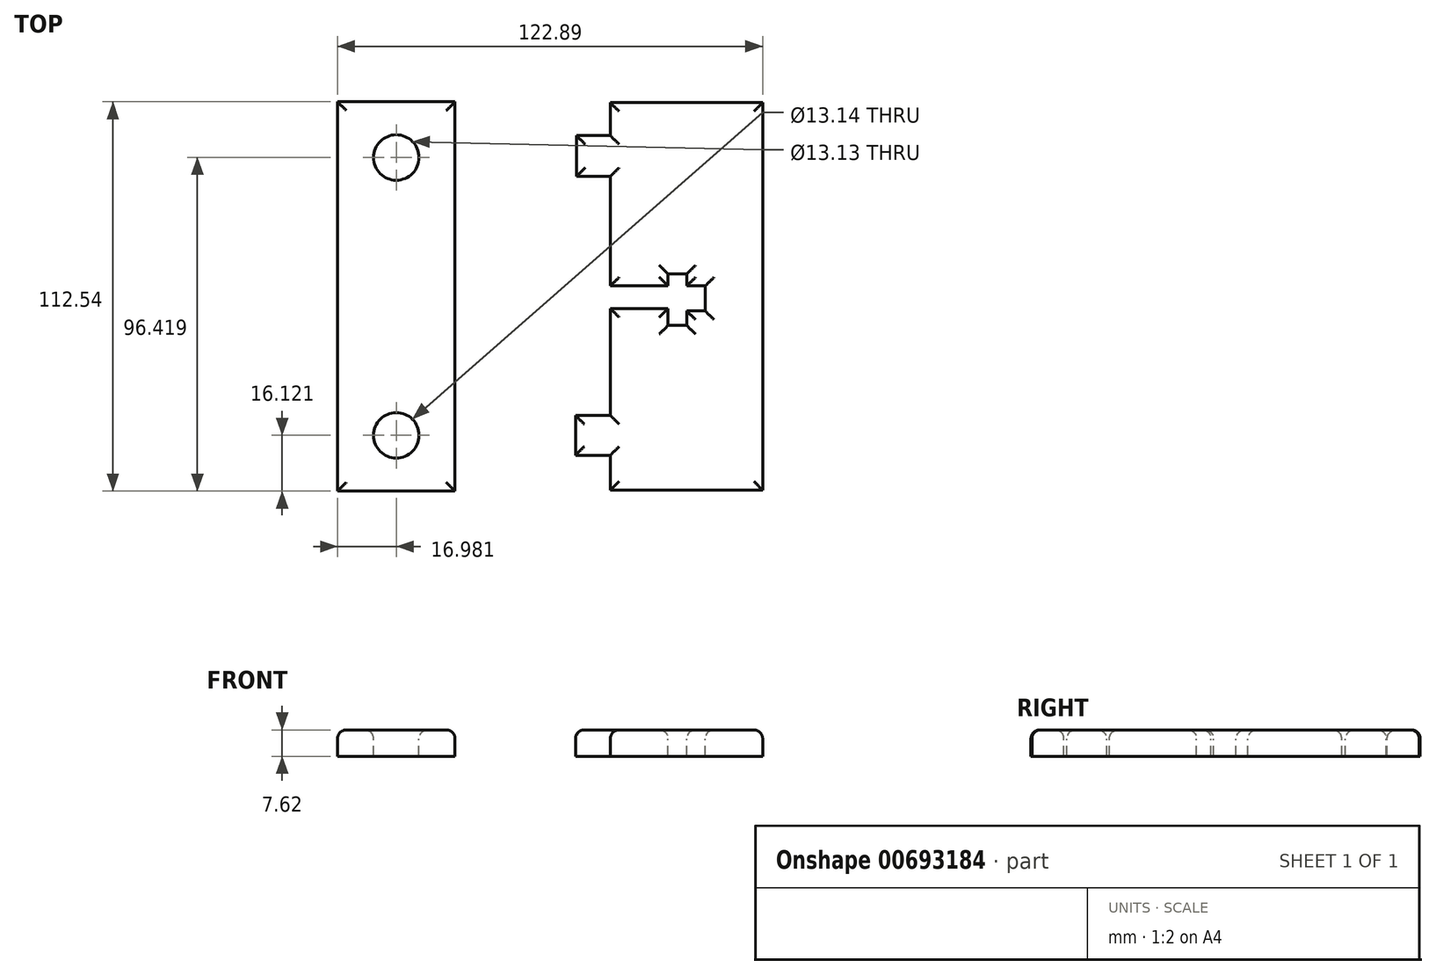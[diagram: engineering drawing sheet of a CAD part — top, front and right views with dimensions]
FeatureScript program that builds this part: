
annotation { "Feature Type Name" : "Feature", "Feature Type Description" : "" }
export const myFeature = defineFeature(function(context is Context, id is Id, definition is map)
    precondition{}
    {
        {
            var Q0;
            Q0=qCreatedBy(makeId("Top.planeOp"),FACE);
            var sketch = newSketch(context, id + "F0", { "sketchPlane" : qUnion([Q0])});
            skLineSegment(sketch, "E0.bottom", {"start": v(-59.72, 56.27) * mm, "end": v(-25.76, 56.27) * mm});
            skLineSegment(sketch, "E0.top", {"start": v(-59.72, -56.27) * mm, "end": v(-25.76, -56.27) * mm});
            skLineSegment(sketch, "E0.left", {"start": v(-59.72, 56.27) * mm, "end": v(-59.72, -56.27) * mm});
            skLineSegment(sketch, "E0.right", {"start": v(-25.76, 56.27) * mm, "end": v(-25.76, -56.27) * mm});
            skCircle(sketch, "E1", {"center": v(-42.74, -40.15) * mm, "radius": 6.57 * mm});
            skCircle(sketch, "E2", {"center": v(-42.74, 40.15) * mm, "radius": 6.56 * mm});
            skLineSegment(sketch, "E3.bottom", {"start": v(19.14, 55.98) * mm, "end": v(63.17, 55.98) * mm});
            skLineSegment(sketch, "E3.top", {"start": v(19.14, -55.98) * mm, "end": v(63.17, -55.98) * mm});
            skLineSegment(sketch, "E3.right", {"start": v(63.17, 55.98) * mm, "end": v(63.17, -55.98) * mm});
            skLineSegment(sketch, "E4", {"start": v(19.14, 46.48) * mm, "end": v(19.14, 55.98) * mm});
            skLineSegment(sketch, "E5", {"start": v(19.14, -55.98) * mm, "end": v(19.14, -45.9) * mm});
            skLineSegment(sketch, "E6", {"start": v(19.14, -45.9) * mm, "end": v(9.07, -45.9) * mm});
            skLineSegment(sketch, "E7", {"start": v(9.07, -45.9) * mm, "end": v(9.07, -34.4) * mm});
            skLineSegment(sketch, "E8", {"start": v(9.07, -34.4) * mm, "end": v(19.14, -34.4) * mm});
            skLineSegment(sketch, "E9", {"start": v(19.14, 46.48) * mm, "end": v(9.35, 46.48) * mm});
            skLineSegment(sketch, "E10", {"start": v(9.35, 46.48) * mm, "end": v(9.35, 34.68) * mm});
            skLineSegment(sketch, "E11", {"start": v(9.35, 34.68) * mm, "end": v(19.14, 34.68) * mm});
            skLineSegment(sketch, "E12", {"start": v(19.14, 3.02) * mm, "end": v(35.83, 3.02) * mm});
            skLineSegment(sketch, "E13", {"start": v(35.83, 3.02) * mm, "end": v(35.83, 6.48) * mm});
            skLineSegment(sketch, "E14", {"start": v(35.83, 6.48) * mm, "end": v(41.24, 6.48) * mm});
            skLineSegment(sketch, "E15", {"start": v(41.24, 6.48) * mm, "end": v(41.24, 3.02) * mm});
            skLineSegment(sketch, "E16", {"start": v(41.24, 3.02) * mm, "end": v(46.56, 3.02) * mm});
            skLineSegment(sketch, "E17", {"start": v(46.56, 3.02) * mm, "end": v(46.56, -2.33) * mm});
            skLineSegment(sketch, "E18", {"start": v(46.56, -2.33) * mm, "end": v(46.56, -4.2) * mm});
            skLineSegment(sketch, "E19", {"start": v(46.56, -4.2) * mm, "end": v(41.24, -4.2) * mm});
            skLineSegment(sketch, "E20", {"start": v(41.24, -4.2) * mm, "end": v(41.24, -8.37) * mm});
            skLineSegment(sketch, "E21", {"start": v(41.24, -8.37) * mm, "end": v(35.83, -8.37) * mm});
            skLineSegment(sketch, "E22", {"start": v(35.83, -8.37) * mm, "end": v(35.83, -3.48) * mm});
            skLineSegment(sketch, "E23", {"start": v(35.83, -3.48) * mm, "end": v(19.14, -3.48) * mm});
            skLineSegment(sketch, "E24", {"start": v(19.14, 3.02) * mm, "end": v(19.14, 34.68) * mm});
            skLineSegment(sketch, "E25", {"start": v(19.14, -3.48) * mm, "end": v(19.14, -34.4) * mm});
            skSolve(sketch);
        }
        {
            var Q0;
            Q0 = qSketchRegion(id + "F0", true);
            var Q1;
            Q1=qCreatedBy(makeId("Front.planeOp"),FACE);
            extrude(context, id + "F1", {"entities" : qUnion([Q0]), "oppositeDirection" : true, "depth" : 7.62 * mm, "endBoundEntityFace" : qUnion([Q1]), "offsetDistance" : 25.4 * mm});
        }
        {
            var Q0;
            Q0=makeQuery(id+"F1.opExtrude","CAP_FACE",FACE,{"disambiguationData":[OSD([sQuery(id+"F0.wireOp",EDGE,"E3.bottom"),sQuery(id+"F0.wireOp",EDGE,"E3.top"),sQuery(id+"F0.wireOp",EDGE,"E3.right"),sQuery(id+"F0.wireOp",EDGE,"E4"),sQuery(id+"F0.wireOp",EDGE,"E5"),sQuery(id+"F0.wireOp",EDGE,"E6"),sQuery(id+"F0.wireOp",EDGE,"E7"),sQuery(id+"F0.wireOp",EDGE,"E8"),sQuery(id+"F0.wireOp",EDGE,"E9"),sQuery(id+"F0.wireOp",EDGE,"E10"),sQuery(id+"F0.wireOp",EDGE,"E11"),sQuery(id+"F0.wireOp",EDGE,"E12"),sQuery(id+"F0.wireOp",EDGE,"E13"),sQuery(id+"F0.wireOp",EDGE,"E14"),sQuery(id+"F0.wireOp",EDGE,"E15"),sQuery(id+"F0.wireOp",EDGE,"E16"),sQuery(id+"F0.wireOp",EDGE,"E17"),sQuery(id+"F0.wireOp",EDGE,"E18"),sQuery(id+"F0.wireOp",EDGE,"E19"),sQuery(id+"F0.wireOp",EDGE,"E20"),sQuery(id+"F0.wireOp",EDGE,"E21"),sQuery(id+"F0.wireOp",EDGE,"E22"),sQuery(id+"F0.wireOp",EDGE,"E23"),sQuery(id+"F0.wireOp",EDGE,"E24"),sQuery(id+"F0.wireOp",EDGE,"E25")])],"isStart":true});
            fillet(context, id + "F2", {"entities" : qUnion([Q0]), "radius" : 2.54 * mm, "tangentPropagation" : true, "allowEdgeOverflow" : false});
        }
        {
            var Q0;
            Q0=makeQuery(id+"F1.opExtrude","CAP_FACE",FACE,{"disambiguationData":[OSD([sQuery(id+"F0.wireOp",EDGE,"E0.bottom"),sQuery(id+"F0.wireOp",EDGE,"E0.top"),sQuery(id+"F0.wireOp",EDGE,"E0.left"),sQuery(id+"F0.wireOp",EDGE,"E0.right"),sQuery(id+"F0.wireOp",EDGE,"E1"),sQuery(id+"F0.wireOp",EDGE,"E2")])],"isStart":true});
            fillet(context, id + "F3", {"entities" : qUnion([Q0]), "radius" : 2.54 * mm, "tangentPropagation" : true, "allowEdgeOverflow" : false});
        }
    });
